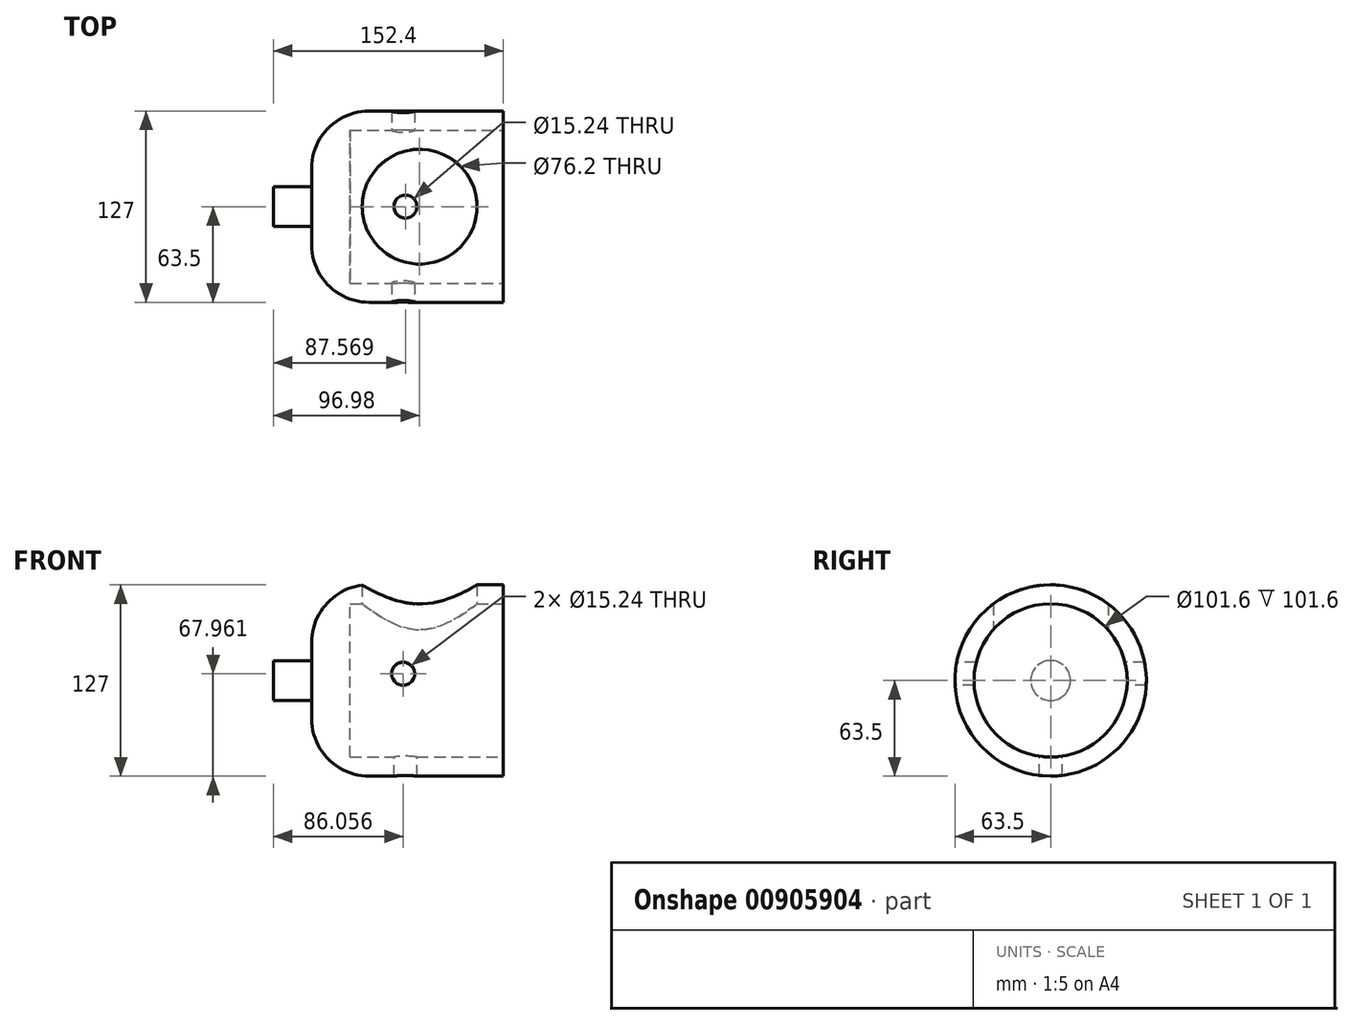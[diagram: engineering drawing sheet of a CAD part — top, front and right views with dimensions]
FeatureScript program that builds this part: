
annotation { "Feature Type Name" : "Feature", "Feature Type Description" : "" }
export const myFeature = defineFeature(function(context is Context, id is Id, definition is map)
    precondition{}
    {
        {
            var Q0;
            Q0=qCreatedBy(makeId("Right.planeOp"),FACE);
            var sketch = newSketch(context, id + "F0", { "sketchPlane" : qUnion([Q0])});
            skCircle(sketch, "E0", {"center": v(0, 0) * mm, "radius": 63.5 * mm});
            skSolve(sketch);
        }
        {
            var Q0;
            Q0=makeQuery(id+"F0.imprint","IMPRINT",FACE,{"disambiguationData":[TD([[makeQuery(id+"F0.imprint","IMPRINT",EDGE,{"derivedFrom":sQuery(id+"F0.wireOp",EDGE,"E0")}),1.0]])]});
            extrude(context, id + "F1", {"entities" : qUnion([Q0]), "depth" : 127 * mm, "offsetDistance" : 25.4 * mm});
        }
        {
            var Q0;
            Q0=makeQuery(id+"F1.opExtrude","CAP_FACE",FACE,{"disambiguationData":[OSD([sQuery(id+"F0.wireOp",EDGE,"E0")])],"isStart":false});
            var sketch = newSketch(context, id + "F2", { "sketchPlane" : qUnion([Q0])});
            skCircle(sketch, "E1", {"center": v(0, 0) * mm, "radius": 50.8 * mm});
            skSolve(sketch);
        }
        {
            var Q0;
            Q0=makeQuery(id+"F2.imprint","IMPRINT",FACE,{"disambiguationData":[TD([[makeQuery(id+"F2.imprint","IMPRINT",EDGE,{"derivedFrom":sQuery(id+"F2.wireOp",EDGE,"E1")}),1.0]])]});
            extrude(context, id + "F3", {"entities" : qUnion([Q0]), "operationType" : NewBodyOperationType.REMOVE, "oppositeDirection" : true, "depth" : 101.6 * mm, "offsetDistance" : 25.4 * mm});
        }
        {
            var Q0;
            Q0=makeQuery(id+"F1.opExtrude","CAP_EDGE",EDGE,{"disambiguationData":[OSD([sQuery(id+"F0.wireOp",EDGE,"E0")])],"isStart":true});
            fillet(context, id + "F4", {"entities" : qUnion([Q0]), "radius" : 38.1 * mm, "tangentPropagation" : true, "allowEdgeOverflow" : false});
        }
        {
            var Q0;
            Q0=qCreatedBy(makeId("Front.planeOp"),FACE);
            cPlane(context, id + "F5", {"entities" : qUnion([Q0]), "cplaneType" : CPlaneType.OFFSET, "offset" : 76.2 * mm, "width" : 152.4 * mm, "height" : 152.4 * mm});
        }
        {
            var Q0;
            Q0=qCreatedBy(id+"F5.planeOp",FACE);
            var sketch = newSketch(context, id + "F6", { "sketchPlane" : qUnion([Q0])});
            skCircle(sketch, "E2", {"center": v(60.66, 4.46) * mm, "radius": 7.62 * mm});
            skSolve(sketch);
        }
        {
            var Q0;
            Q0=makeQuery(id+"F6.imprint","IMPRINT",FACE,{"disambiguationData":[TD([[makeQuery(id+"F6.imprint","IMPRINT",EDGE,{"derivedFrom":sQuery(id+"F6.wireOp",EDGE,"E2")}),1.0]])]});
            extrude(context, id + "F7", {"entities" : qUnion([Q0]), "operationType" : NewBodyOperationType.REMOVE, "oppositeDirection" : true, "depth" : 152.4 * mm, "offsetDistance" : 25.4 * mm});
        }
        {
            var Q0;
            Q0=qCreatedBy(makeId("Top.planeOp"),FACE);
            var sketch = newSketch(context, id + "F8", { "sketchPlane" : qUnion([Q0])});
            skCircle(sketch, "E3", {"center": v(62.17, 0) * mm, "radius": 7.62 * mm});
            skSolve(sketch);
        }
        {
            var Q0;
            Q0 = qSketchRegion(id + "F8", true);
            extrude(context, id + "F9", {"entities" : qUnion([Q0]), "operationType" : NewBodyOperationType.REMOVE, "oppositeDirection" : true, "depth" : 381 * mm, "offsetDistance" : 25.4 * mm});
        }
        {
            var Q0;
            Q0=qCreatedBy(makeId("Top.planeOp"),FACE);
            var sketch = newSketch(context, id + "F10", { "sketchPlane" : qUnion([Q0])});
            skCircle(sketch, "E4", {"center": v(71.58, 0) * mm, "radius": 38.1 * mm});
            skSolve(sketch);
        }
        {
            var Q0;
            Q0 = qSketchRegion(id + "F10", true);
            extrude(context, id + "F11", {"entities" : qUnion([Q0]), "operationType" : NewBodyOperationType.REMOVE, "depth" : 381 * mm, "offsetDistance" : 25.4 * mm});
        }
        {
            var Q0;
            Q0=makeQuery(id+"F1.opExtrude","CAP_FACE",FACE,{"disambiguationData":[OSD([sQuery(id+"F0.wireOp",EDGE,"E0")])],"isStart":true});
            var sketch = newSketch(context, id + "F12", { "sketchPlane" : qUnion([Q0])});
            skCircle(sketch, "E5", {"center": v(0, 0) * mm, "radius": 13.22 * mm});
            skSolve(sketch);
        }
        {
            var Q0;
            Q0 = qSketchRegion(id + "F12", true);
            extrude(context, id + "F13", {"entities" : qUnion([Q0]), "operationType" : NewBodyOperationType.ADD, "depth" : 25.4 * mm, "offsetDistance" : 25.4 * mm});
        }
    });
